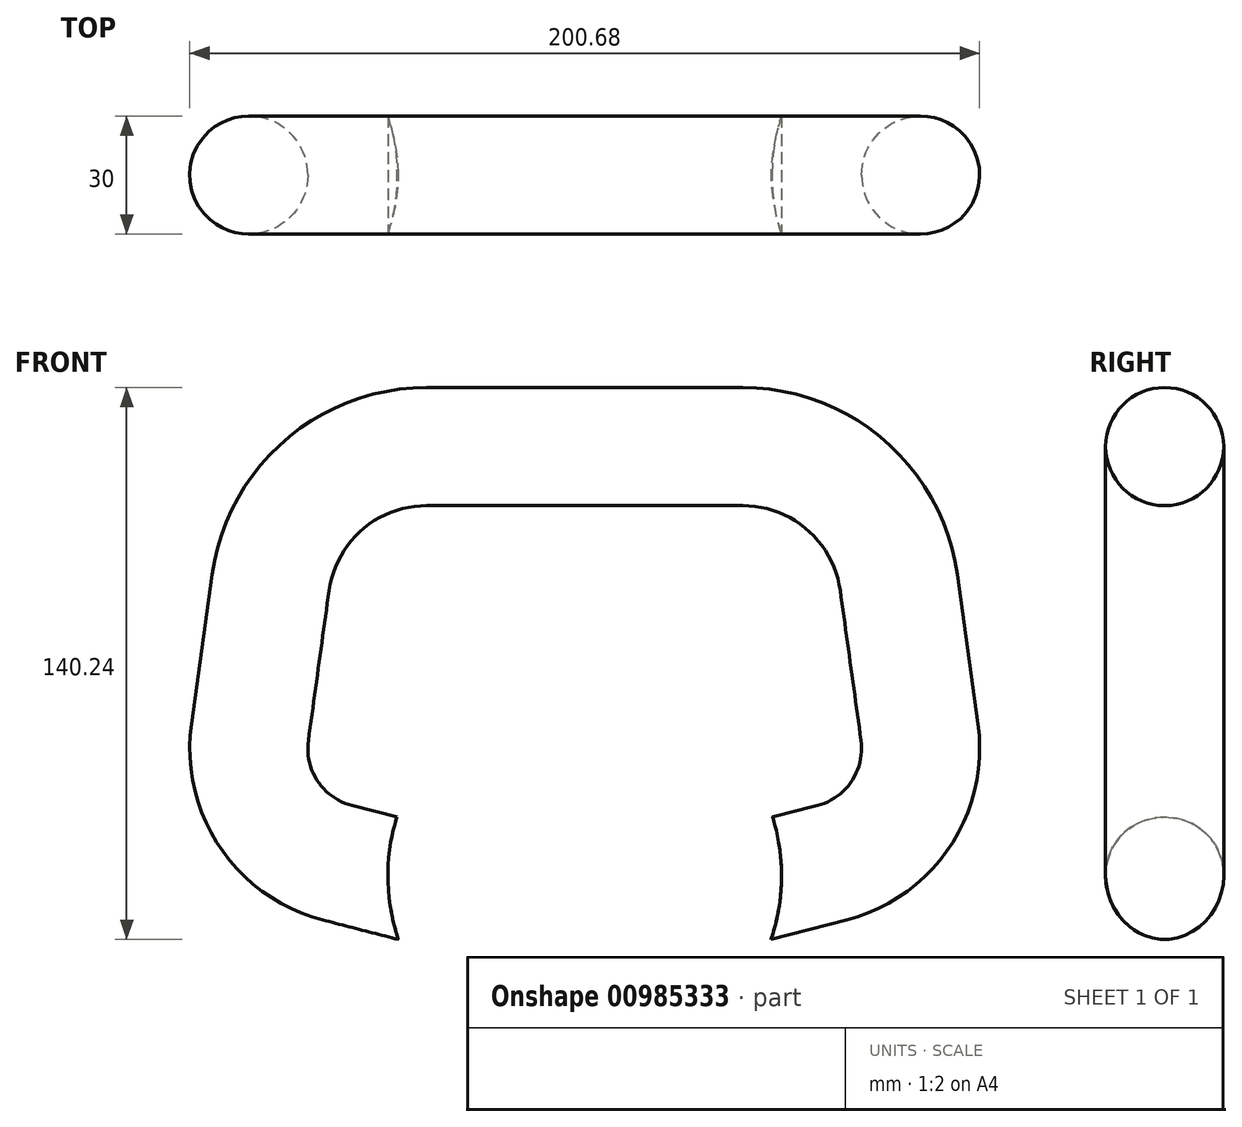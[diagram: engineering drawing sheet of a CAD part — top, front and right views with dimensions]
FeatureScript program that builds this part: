
annotation { "Feature Type Name" : "Feature", "Feature Type Description" : "" }
export const myFeature = defineFeature(function(context is Context, id is Id, definition is map)
    precondition{}
    {
        {
            var Q0;
            Q0=qCreatedBy(makeId("Front.planeOp"),FACE);
            var sketch = newSketch(context, id + "F0", { "sketchPlane" : qUnion([Q0])});
            skCircle(sketch, "E0", {"center": v(0, 0) * mm, "radius": 50 * mm});
            skLineSegment(sketch, "E1", {"start": v(0, -12.9) * mm, "end": v(-62.84, 3.32) * mm});
            skLineSegment(sketch, "E2", {"start": v(-85.06, 36.48) * mm, "end": v(-79.78, 74.54) * mm});
            skLineSegment(sketch, "E3", {"start": v(0, 109.05) * mm, "end": v(40.16, 109.05) * mm});
            skLineSegment(sketch, "E4", {"start": v(79.78, 74.54) * mm, "end": v(85.06, 36.48) * mm});
            skLineSegment(sketch, "E5", {"start": v(62.84, 3.32) * mm, "end": v(0, -12.9) * mm});
            skLineSegment(sketch, "E6", {"start": v(0, 0) * mm, "end": v(0, 109.05) * mm, "construction": true});
            skPoint(sketch, "E7.visualSharp", {"position": v(-75, 109.05) * mm});
            skArc(sketch, "E7.filletArc", {"start": v(-40.16, 109.05) * mm, "mid": v(-66.43, 99.22) * mm, "end": v(-79.78, 74.54) * mm});
            skPoint(sketch, "E8.visualSharp", {"position": v(75, 109.05) * mm});
            skArc(sketch, "E8.filletArc", {"start": v(79.78, 74.54) * mm, "mid": v(66.43, 99.22) * mm, "end": v(40.16, 109.05) * mm});
            skPoint(sketch, "E9.visualSharp", {"position": v(-88.73, 10) * mm});
            skArc(sketch, "E9.filletArc", {"start": v(-85.06, 36.48) * mm, "mid": v(-80.27, 15.67) * mm, "end": v(-62.84, 3.32) * mm});
            skPoint(sketch, "E10.visualSharp", {"position": v(88.73, 10) * mm});
            skArc(sketch, "E10.filletArc", {"start": v(62.84, 3.32) * mm, "mid": v(80.27, 15.67) * mm, "end": v(85.06, 36.48) * mm});
            skLineSegment(sketch, "E11", {"start": v(0, 109.05) * mm, "end": v(-40.16, 109.05) * mm});
            skPoint(sketch, "E12.orphan", {"position": v(-50, 0) * mm});
            skPoint(sketch, "E13.orphan", {"position": v(50, 0) * mm});
            skSolve(sketch);
        }
        {
            var Q0;
            Q0=qCreatedBy(makeId("Right.planeOp"),FACE);
            var sketch = newSketch(context, id + "F1", { "sketchPlane" : qUnion([Q0])});
            skCircle(sketch, "E14", {"center": v(0, 109.05) * mm, "radius": 15 * mm});
            skSolve(sketch);
        }
        {
            var Q0;
            Q0=makeQuery(id+"F1.imprint","IMPRINT",FACE,{"disambiguationData":[TD([[makeQuery(id+"F1.imprint","IMPRINT",EDGE,{"derivedFrom":sQuery(id+"F1.wireOp",EDGE,"E14")}),1.0]])]});
            var Q1;
            Q1=sQuery(id+"F0.wireOp",EDGE,"E1");
            var Q2;
            Q2=sQuery(id+"F0.wireOp",EDGE,"E9.filletArc");
            var Q3;
            Q3=sQuery(id+"F0.wireOp",EDGE,"E2");
            var Q4;
            Q4=sQuery(id+"F0.wireOp",EDGE,"E7.filletArc");
            var Q5;
            Q5=sQuery(id+"F0.wireOp",EDGE,"E11");
            sweep(context, id + "F2", {"profiles" : qUnion([Q0]), "path" : qUnion([Q1, Q2, Q3, Q4, Q5])});
        }
        {
            var Q0;
            Q0=qSketchRegion(id+"F1",true);
            var Q1;
            Q1=sQuery(id+"F0.wireOp",EDGE,"E3");
            var Q2;
            Q2=sQuery(id+"F0.wireOp",EDGE,"E8.filletArc");
            var Q3;
            Q3=sQuery(id+"F0.wireOp",EDGE,"E4");
            var Q4;
            Q4=sQuery(id+"F0.wireOp",EDGE,"E10.filletArc");
            var Q5;
            Q5=sQuery(id+"F0.wireOp",EDGE,"E5");
            sweep(context, id + "F3", {"operationType" : NewBodyOperationType.ADD, "profiles" : qUnion([Q0]), "path" : qUnion([Q1, Q2, Q3, Q4, Q5])});
        }
        {
            var Q0;
            {var subQ0=sQuery(id+"F0.wireOp",EDGE,"E1");var subQ1=sQuery(id+"F0.wireOp",EDGE,"E0");var subQ2=makeQuery(id+"F0.imprint","INTERSECT",VERTEX,{"derivedFrom":[subQ1,subQ0]});Q0=makeQuery(id+"F0.imprint","IMPRINT",FACE,{"disambiguationData":[TD([[makeQuery(id+"F0.imprint","IMPRINT",EDGE,{"disambiguationData":[TD([[subQ2,1.0]])],"derivedFrom":subQ1}),1.0]])]});}
            var Q1;
            {var subQ0=sQuery(id+"F0.wireOp",EDGE,"E1");var subQ1=sQuery(id+"F0.wireOp",EDGE,"E0");var subQ2=makeQuery(id+"F0.imprint","INTERSECT",VERTEX,{"derivedFrom":[subQ1,subQ0]});Q1=makeQuery(id+"F0.imprint","IMPRINT",FACE,{"disambiguationData":[TD([[makeQuery(id+"F0.imprint","IMPRINT",EDGE,{"disambiguationData":[TD([[subQ2,-1.0]])],"derivedFrom":subQ1}),1.0]])]});}
            extrude(context, id + "F4", {"entities" : qUnion([Q0, Q1]), "operationType" : NewBodyOperationType.REMOVE, "endBound" : BoundingType.THROUGH_ALL, "oppositeDirection" : true, "depth" : 25 * mm, "hasSecondDirection" : true, "secondDirectionBound" : SecondDirectionBoundingType.THROUGH_ALL, "secondDirectionOppositeDirection" : false, "secondDirectionDepth" : 25 * mm});
        }
    });
